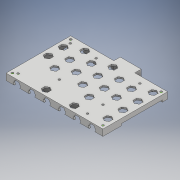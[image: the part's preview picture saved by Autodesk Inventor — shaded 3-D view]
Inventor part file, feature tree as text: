
AUTODESK INVENTOR PART (.ipt)
format: ipt  version: 2017 (Build 210142000, 142)  size: 1,346,560 bytes
history: native  units: mm
features: extrude x28, sketch x28, projected_geometry x22, draft x2
ambient origin geometry x8: Origin, YZ Plane, XZ Plane, XY Plane, X Axis, Y Axis, Z Axis, Center Point
bodies: Solid1 (feature_tree)
feature tree (80):
  extrude  "Extrusion1"  Depth=3.0mm
  extrude  "Extrusion2"  Depth=56.0mm
  draft  "FaceDraft1"
  draft  "FaceDraft2"
  extrude  "Extrusion3"  Depth=3.5mm
  extrude  "Extrusion4"  Depth=2.75mm
  extrude  "Extrusion5"  Depth=2.75mm
  extrude  "Extrusion7"  Depth=0.5mm
  extrude  "Extrusion8"  Depth=32.0mm
  extrude  "Extrusion9"  Depth=24.0mm
  extrude  "Extrusion10"  Depth=5.5mm
  extrude  "Extrusion11"  Depth=2.0mm TaperAngle=0.0deg
  extrude  "Extrusion12"  Depth=49.0mm
  extrude  "Extrusion13"  Depth=69.5mm
  extrude  "Extrusion14"  Depth=92.45mm
  extrude  "Extrusion15"  Depth=69.5mm
  extrude  "Extrusion16"  Depth=2.75mm
  extrude  "Extrusion17"  Depth=1.0mm
  extrude  "Extrusion18"  Depth=88.0mm
  extrude  "Extrusion25"  Depth=6.0mm
  extrude  "Extrusion27"  Depth=6.0mm
  extrude  "Extrusion28"  Depth=3.0mm TaperAngle=0.0deg
  extrude  "Extrusion29"  TaperAngle=15.0deg  [1 undecoded]
  extrude  "Extrusion32"  Depth=6.0mm
  extrude  "Extrusion33"  Depth=6.0mm
  extrude  "Extrusion35"  Depth=5.5mm
  extrude  "Extrusion37"  Depth=1.0mm
  extrude  "Extrusion38"  Depth=14.0mm TaperAngle=0.0deg
  extrude  "Extrusion39"  Depth=28.0mm
  sketch  "Sketch50"  dims[d163=2.75mm d172=28.0mm]
  extrude  "Extrusion43"  Depth=3.0mm TaperAngle=0.0deg
  sketch  "Sketch1"  dims[d1=78.0mm d3=3.0mm]
  sketch  "Sketch2"  dims[d7=85.0mm d8=56.0mm]
  sketch  "Sketch3"  dims[d9=3.5mm d10=3.5mm]
  sketch  "Sketch4"  dims[d11=49.0mm d12=2.75mm]
  sketch  "Sketch5"  dims[d13=2.75mm d14=2.75mm]
  sketch  "Sketch8"  dims[d21=0.5mm d22=0.5mm]
  projected_geometry  "Projected Loop1"
  sketch  "Sketch9"  dims[d23=0.5mm d24=32.0mm]
  projected_geometry  "Projected Loop2"
  sketch  "Sketch10"  dims[d25=12.0mm d28=24.0mm]
  sketch  "Sketch11"  dims[d29=10.6mm d30=5.5mm]
  sketch  "Sketch13"  dims[d31=11.0mm d32=2.0mm d33=2.0mm d34=0.0mm]
  projected_geometry  "Projected Loop3"
  projected_geometry  "Projected Loop4"
  projected_geometry  "Projected Loop5"
  sketch  "Sketch15"  dims[d45=58.0mm d46=49.0mm]
  sketch  "Sketch16"  dims[d47=2.75mm d48=69.5mm]
  sketch  "Sketch17"  dims[d49=90.0deg d50=92.45mm]
  sketch  "Sketch18"  dims[d51=90.0deg d52=69.5mm]
  projected_geometry  "Projected Loop10"
  projected_geometry  "Projected Loop11"
  projected_geometry  "Projected Loop12"
  projected_geometry  "Projected Loop13"
  sketch  "Sketch20"  dims[d53=90.0deg d55=2.75mm]
  sketch  "Sketch21"  dims[d56=1.0mm d57=21.0mm]
  sketch  "Sketch29"  dims[d64=5.1mm d65=88.0mm]
  sketch  "Sketch33"  dims[d66=90.0deg d67=6.0mm]
  projected_geometry  "Projected Loop20"
  sketch  "Sketch34"  dims[d68=6.0mm d69=6.0mm]
  projected_geometry  "Projected Loop21"
  sketch  "Sketch35"  dims[d70=6.0mm d71=3.0mm d72=0.0mm]
  projected_geometry  "Projected Loop22"
  projected_geometry  "Projected Loop23"
  projected_geometry  "Projected Loop24"
  sketch  "Sketch38"  dims[d73=15.0deg d74=15.0deg]
  sketch  "Sketch39"  dims[d111=2.75mm d112=6.0mm]
  projected_geometry  "Projected Loop27"
  sketch  "Sketch41"  dims[d113=6.0mm d114=6.0mm]
  projected_geometry  "Projected Loop33"
  projected_geometry  "Projected Loop34"
  projected_geometry  "Projected Loop35"
  projected_geometry  "Projected Loop36"
  projected_geometry  "Projected Loop37"
  sketch  "Sketch43"  dims[d152=6.0mm d153=0.0mm d154=5.5mm]
  sketch  "Sketch44"  dims[d155=1.0mm d156=1.0mm]
  projected_geometry  "Projected Loop42"
  sketch  "Sketch45"  dims[d157=88.0mm d158=0.0mm d159=14.0mm d160=0.0mm]
  projected_geometry  "Projected Loop46"
  sketch  "Sketch51"  dims[d180=2.0mm d181=4.25mm d182=0.0mm d183=1.0mm d184=1.0mm d185=11.0mm d186=15.98mm d187=0.0mm d188=1.0mm d189=1.0mm d190=11.0mm d191=16.23mm d192=0.0mm d193=7.36mm d194=1.0mm d195=2.0mm d196=0.0mm d197=4.3mm d199=3.0mm d200=2.0mm d201=4.6mm d202=0.0mm d203=2.0mm d204=0.0mm d205=4.3mm d206=3.0mm d207=2.0mm d208=10.0mm d209=0.0mm d210=1.0mm d211=1.0mm d212=11.0mm d213=0.5mm d214=0.0mm d215=1.75mm d216=0.0mm d217=8.5mm d218=0.0mm d222=6.5mm d223=0.0mm d226=11.0mm d227=120.7mm d228=5.0mm d229=110.7mm d231=2.1mm d232=67.4mm d233=2.0mm d234=0.0mm d995=5.0mm d996=10.0mm d997=5.0mm d998=10.0mm d999=5.0mm d1000=10.0mm d1001=5.0mm d1002=5.0mm d1003=10.0mm d1004=5.0mm d1005=5.0mm d1006=10.0mm d1007=5.0mm d1008=10.0mm d1009=5.0mm d1010=10.0mm d1011=5.0mm d1012=10.0mm d1013=5.0mm d1014=10.0mm d1015=5.0mm d1016=10.0mm d1017=5.0mm d1018=10.0mm d1019=5.0mm d1020=10.0mm d1021=5.0mm d1022=10.0mm d1023=5.0mm d1024=10.0mm d1025=5.0mm d1026=10.0mm d1027=5.0mm d1028=5.0mm d1029=5.0mm d1030=5.0mm d1031=10.0mm d1032=5.0mm d1033=10.0mm d1034=5.0mm d1035=5.0mm d1036=10.0mm d1037=5.0mm d1038=10.0mm d1039=10.0mm d1040=5.0mm d1041=10.0mm d1042=5.0mm d1043=10.0mm d1044=5.0mm d1045=10.0mm d1046=3.0mm d1047=0.0mm d1050=0.5mm d1051=0.5mm d1054=0.5mm d1055=0.5mm d1056=0.5mm d1057=0.5mm d1058=87.511mm d1059=0.0mm d1060=12.0mm d1061=0.0mm d1062=92.45mm d1063=3.25mm d1064=4.0mm d1065=0.0mm d1067=0.0mm d1068=1.5mm d1069=0.0mm d1082=4.5mm d1083=4.5mm d1085=4.5mm d1086=4.5mm d1087=2.75mm d1088=4.5mm d1089=4.5mm d1090=2.75mm d1091=6.5mm d1092=0.0mm d1093=4.0mm d1094=0.0mm d1097=10.0mm d1098=0.0mm d1144=34.728mm d1145=2.0mm d1146=0.0mm d1147=2.0mm d1148=0.0mm d1149=0.327mm d1150=90.0deg d1151=2.75mm d1152=3.0mm d1153=3.0mm d1154=3.0mm d1156=0.1mm d1158=90.0deg d1159=150.0mm d1160=0.0mm d1193=2.7mm d1194=2.7mm d1195=2.7mm d1196=2.7mm d1197=2.7mm d1198=3.0mm d1212=4.5mm d1213=4.5mm d1214=4.5mm d1215=4.5mm d1216=4.5mm d1217=4.5mm d1218=4.5mm d1219=4.5mm d1220=3.0mm d1221=0.0mm]
note: 1 required parameter value undecoded (feature->parameter linkage not recoverable at this tier; creation-order binding heuristic only, values carry confidence <= 0.55)
